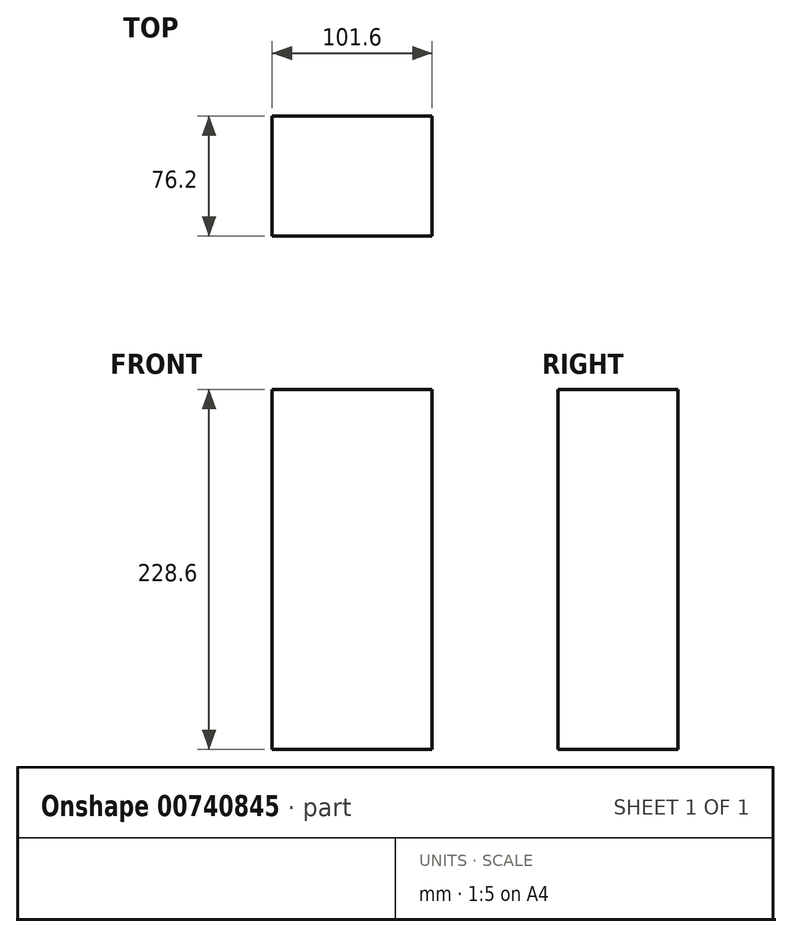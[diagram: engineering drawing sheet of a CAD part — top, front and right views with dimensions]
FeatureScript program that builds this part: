
annotation { "Feature Type Name" : "Feature", "Feature Type Description" : "" }
export const myFeature = defineFeature(function(context is Context, id is Id, definition is map)
    precondition{}
    {
        {
            var Q0;
            Q0=qCreatedBy(makeId("Front.planeOp"),FACE);
            var sketch = newSketch(context, id + "F0", { "sketchPlane" : qUnion([Q0])});
            skLineSegment(sketch, "E0.bottom", {"start": v(-49.06, 149.84) * mm, "end": v(52.54, 149.84) * mm});
            skLineSegment(sketch, "E0.top", {"start": v(-49.06, -78.76) * mm, "end": v(52.54, -78.76) * mm});
            skLineSegment(sketch, "E0.left", {"start": v(-49.06, 149.84) * mm, "end": v(-49.06, -78.76) * mm});
            skLineSegment(sketch, "E0.right", {"start": v(52.54, 149.84) * mm, "end": v(52.54, -78.76) * mm});
            skPoint(sketch, "E0.middle", {"position": v(1.74, 35.54) * mm});
            skSolve(sketch);
        }
        {
            var Q0;
            Q0 = qSketchRegion(id + "F0", true);
            extrude(context, id + "F1", {"entities" : qUnion([Q0]), "depth" : 76.2 * mm, "offsetDistance" : 25.4 * mm});
        }
    });
